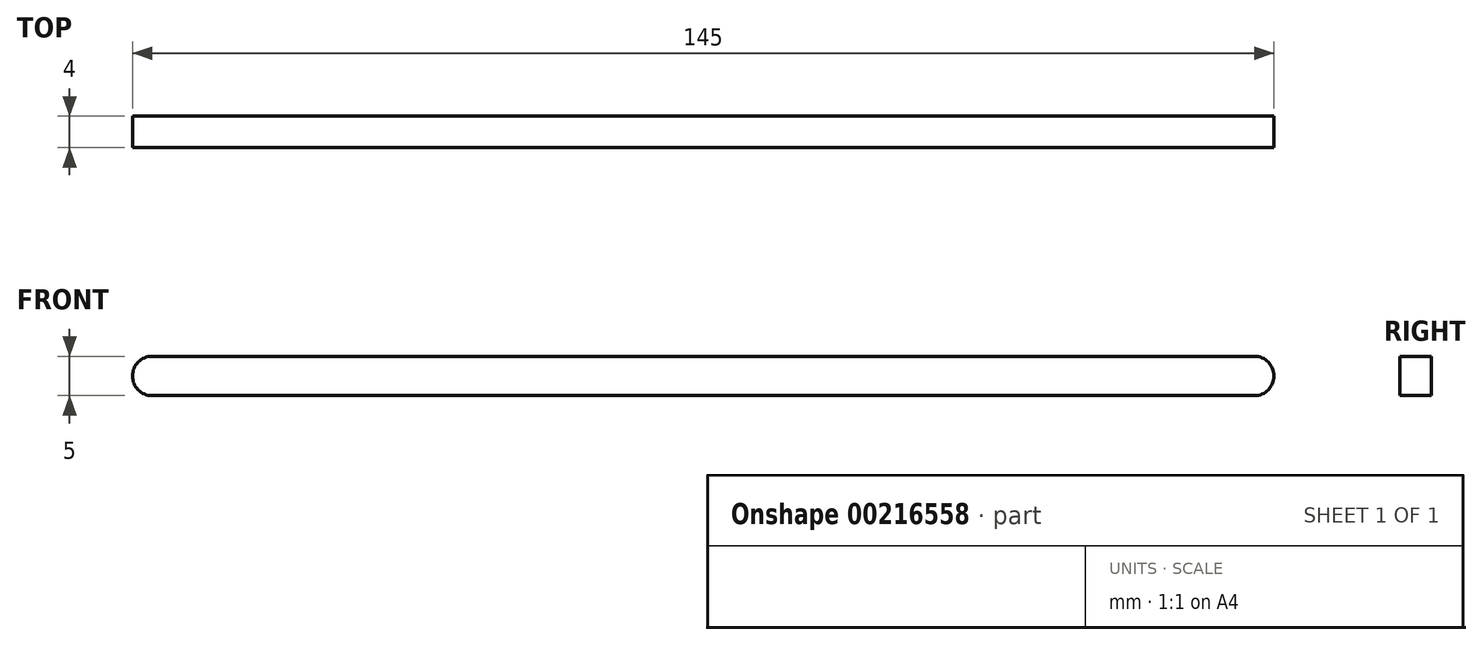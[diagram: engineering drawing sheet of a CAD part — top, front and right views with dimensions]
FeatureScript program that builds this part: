
annotation { "Feature Type Name" : "Feature", "Feature Type Description" : "" }
export const myFeature = defineFeature(function(context is Context, id is Id, definition is map)
    precondition{}
    {
        {
            var Q0;
            Q0=qCreatedBy(makeId("Front.planeOp"),FACE);
            var sketch = newSketch(context, id + "F0", { "sketchPlane" : qUnion([Q0])});
            skLineSegment(sketch, "E0.bottom", {"start": v(-70, 2.5) * mm, "end": v(70, 2.5) * mm});
            skLineSegment(sketch, "E0.top", {"start": v(-70, -2.5) * mm, "end": v(70, -2.5) * mm});
            skPoint(sketch, "E0.middle", {"position": v(0, 0) * mm});
            skArc(sketch, "E1", {"start": v(-70, 2.5) * mm, "mid": v(-72.5, 0) * mm, "end": v(-70, -2.5) * mm});
            skPoint(sketch, "E2", {"position": v(70, 0) * mm});
            skArc(sketch, "E3", {"start": v(70, 2.5) * mm, "mid": v(72.5, 0) * mm, "end": v(70, -2.5) * mm});
            skSolve(sketch);
        }
        {
            var Q0;
            Q0=makeQuery(id+"F0.imprint","IMPRINT",FACE,{"disambiguationData":[TD([[makeQuery(id+"F0.imprint","IMPRINT",EDGE,{"derivedFrom":sQuery(id+"F0.wireOp",EDGE,"E0.bottom")}),-1.0]])]});
            extrude(context, id + "F1", {"entities" : qUnion([Q0]), "depth" : 4 * mm});
        }
    });
